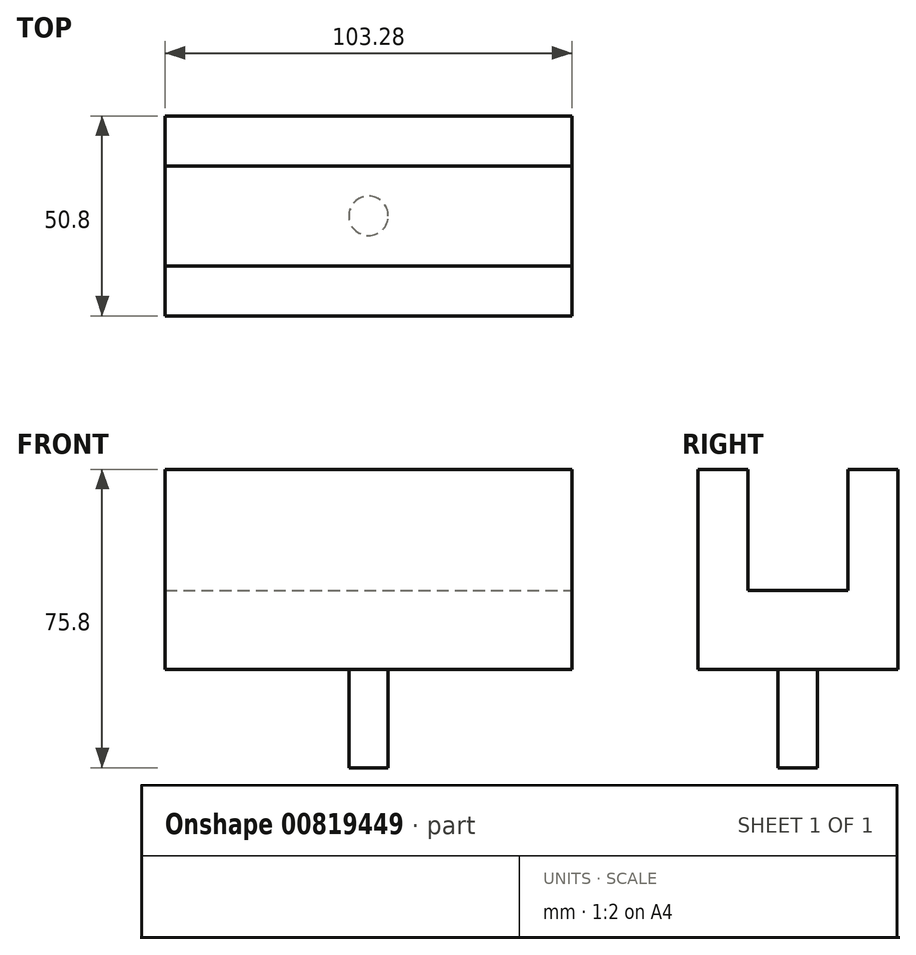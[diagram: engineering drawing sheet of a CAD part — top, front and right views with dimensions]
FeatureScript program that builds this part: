
annotation { "Feature Type Name" : "Feature", "Feature Type Description" : "" }
export const myFeature = defineFeature(function(context is Context, id is Id, definition is map)
    precondition{}
    {
        {
            var Q0;
            Q0=qCreatedBy(makeId("Top.planeOp"),FACE);
            var sketch = newSketch(context, id + "F0", { "sketchPlane" : qUnion([Q0])});
            skLineSegment(sketch, "E0.bottom", {"start": v(51.64, 25.4) * mm, "end": v(-51.64, 25.4) * mm});
            skLineSegment(sketch, "E0.top", {"start": v(51.64, -25.4) * mm, "end": v(-51.64, -25.4) * mm});
            skLineSegment(sketch, "E0.left", {"start": v(51.64, 25.4) * mm, "end": v(51.64, -25.4) * mm});
            skLineSegment(sketch, "E0.right", {"start": v(-51.64, 25.4) * mm, "end": v(-51.64, -25.4) * mm});
            skPoint(sketch, "E0.middle", {"position": v(0, 0) * mm});
            skLineSegment(sketch, "E1", {"start": v(-51.64, 12.7) * mm, "end": v(51.64, 12.7) * mm});
            skLineSegment(sketch, "E2", {"start": v(-51.64, -12.7) * mm, "end": v(51.64, -12.7) * mm});
            skSolve(sketch);
        }
        {
            var Q0;
            {var subQ0=sQuery(id+"F0.wireOp",EDGE,"E0.bottom");Q0=makeQuery(id+"F0.imprint","IMPRINT",FACE,{"disambiguationData":[TD([[makeQuery(id+"F0.imprint","IMPRINT",EDGE,{"derivedFrom":subQ0}),1.0]])]});}
            var Q1;
            {var subQ0=sQuery(id+"F0.wireOp",EDGE,"E0.top");Q1=makeQuery(id+"F0.imprint","IMPRINT",FACE,{"disambiguationData":[TD([[makeQuery(id+"F0.imprint","IMPRINT",EDGE,{"derivedFrom":subQ0}),-1.0]])]});}
            extrude(context, id + "F1", {"entities" : qUnion([Q0, Q1]), "depth" : 50.8 * mm, "offsetDistance" : 25 * mm});
        }
        {
            var Q0;
            {var subQ0=sQuery(id+"F0.wireOp",EDGE,"E1");Q0=makeQuery(id+"F0.imprint","IMPRINT",FACE,{"disambiguationData":[TD([[makeQuery(id+"F0.imprint","IMPRINT",EDGE,{"derivedFrom":subQ0}),-1.0]])]});}
            extrude(context, id + "F2", {"entities" : qUnion([Q0]), "operationType" : NewBodyOperationType.ADD, "depth" : 20 * mm, "offsetDistance" : 25 * mm});
        }
        {
            var Q0;
            {var subQ0=sQuery(id+"F0.wireOp",EDGE,"E1");Q0=makeQuery(id+"F0.imprint","IMPRINT",FACE,{"disambiguationData":[TD([[makeQuery(id+"F0.imprint","IMPRINT",EDGE,{"derivedFrom":subQ0}),-1.0]])]});}
            var sketch = newSketch(context, id + "F3", { "sketchPlane" : qUnion([Q0])});
            skCircle(sketch, "E3", {"center": v(0, 0) * mm, "radius": 5 * mm});
            skSolve(sketch);
        }
        {
            var Q0;
            Q0=makeQuery(id+"F3.imprint","IMPRINT",FACE,{"disambiguationData":[TD([[makeQuery(id+"F3.imprint","IMPRINT",EDGE,{"derivedFrom":sQuery(id+"F3.wireOp",EDGE,"E3")}),1.0]])]});
            extrude(context, id + "F4", {"entities" : qUnion([Q0]), "operationType" : NewBodyOperationType.ADD, "oppositeDirection" : true, "depth" : 25 * mm, "offsetDistance" : 25 * mm});
        }
    });
